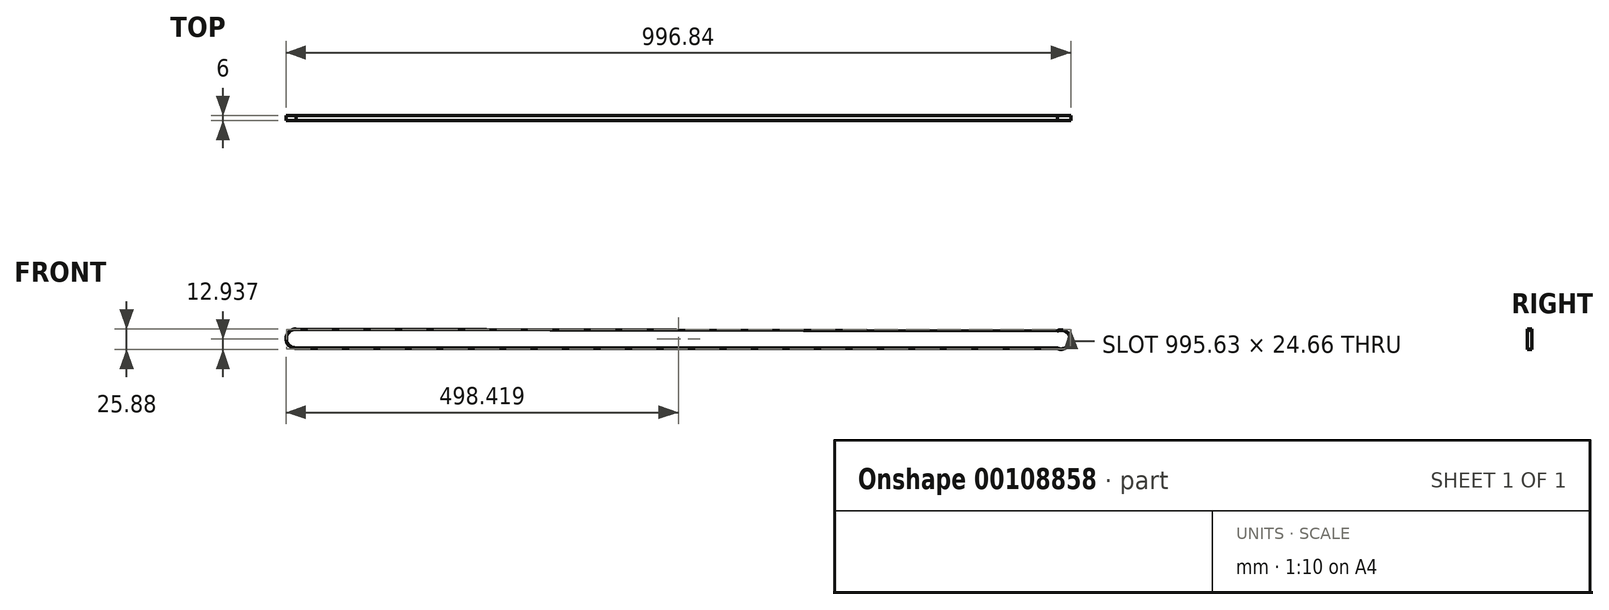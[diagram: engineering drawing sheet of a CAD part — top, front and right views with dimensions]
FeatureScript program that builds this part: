
annotation { "Feature Type Name" : "Feature", "Feature Type Description" : "" }
export const myFeature = defineFeature(function(context is Context, id is Id, definition is map)
    precondition{}
    {
        {
            var Q0;
            Q0=qCreatedBy(makeId("Front.planeOp"),FACE);
            var sketch = newSketch(context, id + "F0", { "sketchPlane" : qUnion([Q0])});
            skArc(sketch, "E0", {"start": v(-79.46, 23.34) * mm, "mid": v(-91.67, 11.98) * mm, "end": v(-80.08, 0) * mm});
            skArc(sketch, "E1", {"start": v(886.92, 0) * mm, "mid": v(903.93, 10.04) * mm, "end": v(887.54, 21.06) * mm});
            skLineSegment(sketch, "E2", {"start": v(-79.46, 23.34) * mm, "end": v(887.54, 21.06) * mm});
            skLineSegment(sketch, "E3", {"start": v(886.92, 0) * mm, "end": v(-80.08, 0) * mm});
            skLineSegment(sketch, "E4", {"start": v(0, -9.6) * mm, "end": v(0, 13.17) * mm, "construction": true});
            skPoint(sketch, "E5", {"position": v(-79.46, 23.34) * mm});
            skSolve(sketch);
        }
        {
            var Q0;
            Q0=qCreatedBy(makeId("Right.planeOp"),FACE);
            cPlane(context, id + "F1", {"entities" : qUnion([Q0]), "cplaneType" : CPlaneType.OFFSET, "offset" : 80 * mm, "oppositeDirection" : true, "width" : 150 * mm, "height" : 150 * mm});
        }
        {
            var Q0;
            Q0=qCreatedBy(id+"F1.planeOp",FACE);
            var sketch = newSketch(context, id + "F2", { "sketchPlane" : qUnion([Q0])});
            skLineSegment(sketch, "E6.bottom", {"start": v(0, 23.37) * mm, "end": v(-3, 23.37) * mm});
            skLineSegment(sketch, "E6.top", {"start": v(0, 23.97) * mm, "end": v(-3, 23.97) * mm});
            skLineSegment(sketch, "E6.left", {"start": v(0, 23.37) * mm, "end": v(0, 23.97) * mm});
            skLineSegment(sketch, "E6.right", {"start": v(-3, 23.37) * mm, "end": v(-3, 23.97) * mm});
            skLineSegment(sketch, "E7", {"start": v(0, 24.75) * mm, "end": v(0, 21.85) * mm, "construction": true});
            skLineSegment(sketch, "E8.MirrorCS", {"start": v(0, 23.37) * mm, "end": v(3, 23.37) * mm});
            skLineSegment(sketch, "E9.MirrorCS", {"start": v(3, 23.37) * mm, "end": v(3, 23.97) * mm});
            skLineSegment(sketch, "E10.MirrorCS", {"start": v(0, 23.97) * mm, "end": v(3, 23.97) * mm});
            skSolve(sketch);
        }
        {
            var Q0;
            Q0=makeQuery(id+"F2.imprint","IMPRINT",FACE,{"disambiguationData":[TD([[makeQuery(id+"F2.imprint","IMPRINT",EDGE,{"derivedFrom":sQuery(id+"F2.wireOp",EDGE,"E6.bottom")}),-1.0]])]});
            var Q1;
            Q1=makeQuery(id+"F2.imprint","IMPRINT",FACE,{"disambiguationData":[TD([[makeQuery(id+"F2.imprint","IMPRINT",EDGE,{"derivedFrom":sQuery(id+"F2.wireOp",EDGE,"E8.MirrorCS")}),1.0]])]});
            var Q2;
            Q2=sQuery(id+"F0.wireOp",EDGE,"E2");
            var Q3;
            Q3=sQuery(id+"F0.wireOp",EDGE,"E0");
            var Q4;
            Q4=sQuery(id+"F0.wireOp",EDGE,"E3");
            var Q5;
            Q5=sQuery(id+"F0.wireOp",EDGE,"E1");
            sweep(context, id + "F3", {"profiles" : qUnion([Q0, Q1]), "path" : qUnion([Q2, Q3, Q4, Q5])});
        }
    });
